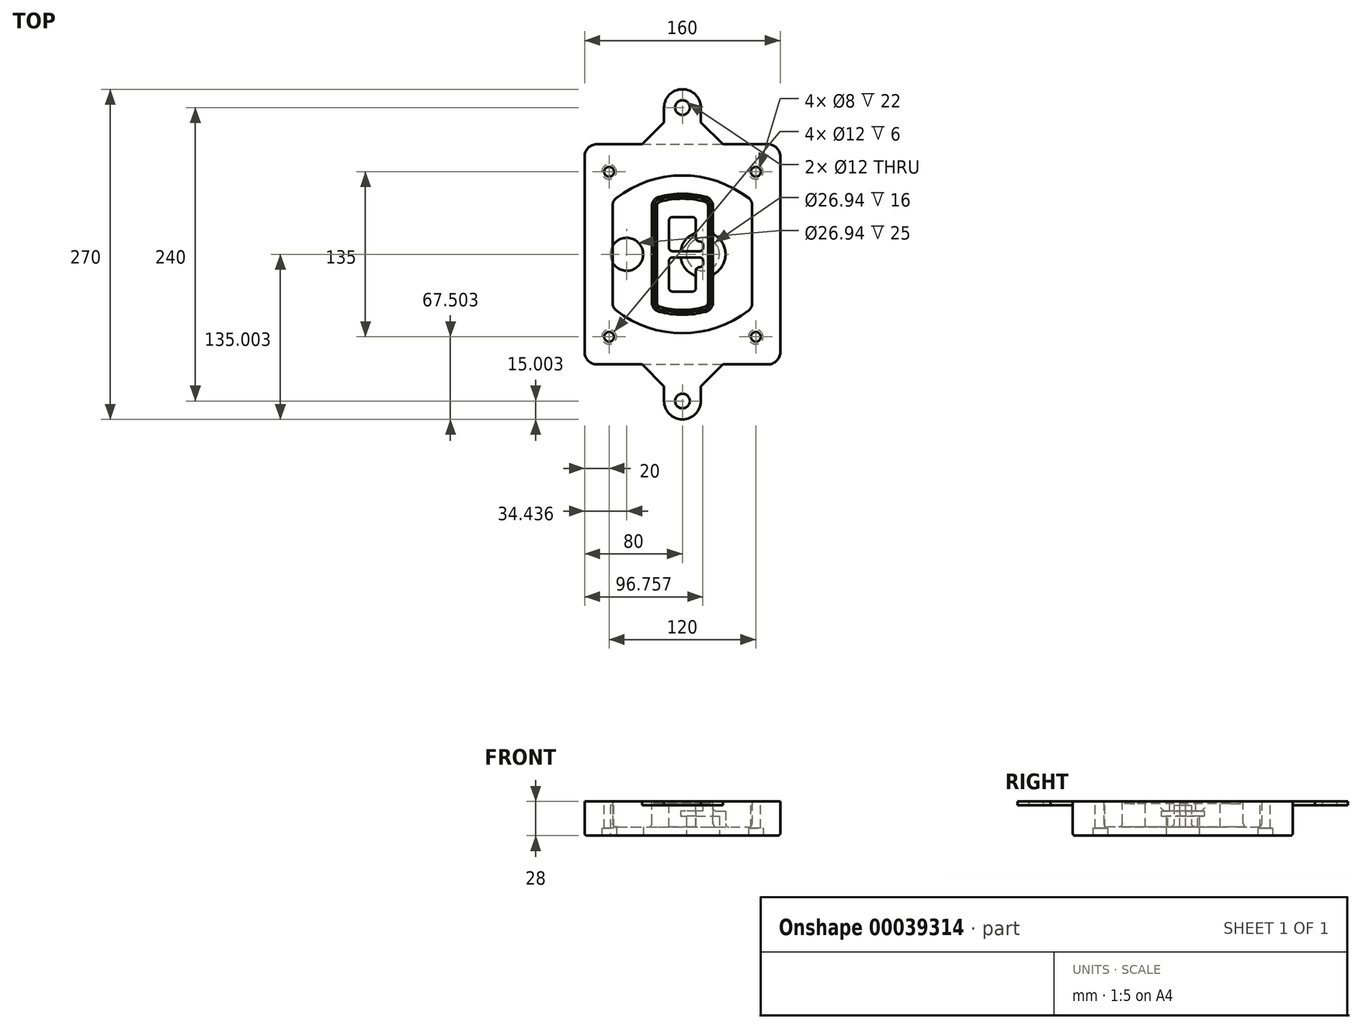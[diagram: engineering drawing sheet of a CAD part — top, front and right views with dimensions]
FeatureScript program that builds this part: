
annotation { "Feature Type Name" : "Feature", "Feature Type Description" : "" }
export const myFeature = defineFeature(function(context is Context, id is Id, definition is map)
    precondition{}
    {
        {
            var Q0;
            Q0=qCreatedBy(makeId("Top.planeOp"),FACE);
            var sketch = newSketch(context, id + "F0", { "sketchPlane" : qUnion([Q0])});
            skPoint(sketch, "E0.rect.middle", {"position": v(0, 0) * mm});
            skLineSegment(sketch, "E1.bottom", {"start": v(24.05, 28.38) * mm, "end": v(164.05, 28.38) * mm});
            skLineSegment(sketch, "E1.top", {"start": v(24.05, 208.38) * mm, "end": v(164.05, 208.38) * mm});
            skLineSegment(sketch, "E1.left", {"start": v(14.05, 38.38) * mm, "end": v(14.05, 198.38) * mm});
            skLineSegment(sketch, "E1.right", {"start": v(174.05, 38.38) * mm, "end": v(174.05, 198.38) * mm});
            skLineSegment(sketch, "E2", {"start": v(14.05, 208.38) * mm, "end": v(174.05, 28.38) * mm, "construction": true});
            skLineSegment(sketch, "E3", {"start": v(174.05, 208.38) * mm, "end": v(14.05, 28.38) * mm, "construction": true});
            skCircle(sketch, "E4", {"center": v(34.05, 185.88) * mm, "radius": 4 * mm});
            skCircle(sketch, "E5", {"center": v(154.05, 185.88) * mm, "radius": 4 * mm});
            skCircle(sketch, "E6", {"center": v(154.05, 50.88) * mm, "radius": 4 * mm});
            skCircle(sketch, "E7", {"center": v(34.05, 50.88) * mm, "radius": 4 * mm});
            skLineSegment(sketch, "E8", {"start": v(34.05, 185.88) * mm, "end": v(154.05, 185.88) * mm, "construction": true});
            skLineSegment(sketch, "E9", {"start": v(154.05, 185.88) * mm, "end": v(154.05, 50.88) * mm, "construction": true});
            skLineSegment(sketch, "E10", {"start": v(154.05, 50.88) * mm, "end": v(34.05, 50.88) * mm, "construction": true});
            skLineSegment(sketch, "E11", {"start": v(34.05, 50.88) * mm, "end": v(34.05, 185.88) * mm, "construction": true});
            skLineSegment(sketch, "E12", {"start": v(34.05, 158.68) * mm, "end": v(34.05, 78.09) * mm});
            skLineSegment(sketch, "E13", {"start": v(154.05, 158.68) * mm, "end": v(154.05, 78.09) * mm});
            skArc(sketch, "E14", {"start": v(150.2, 166.56) * mm, "mid": v(94.05, 185.88) * mm, "end": v(37.9, 166.56) * mm});
            skArc(sketch, "E15", {"start": v(37.9, 70.2) * mm, "mid": v(94.05, 50.88) * mm, "end": v(150.2, 70.2) * mm});
            skLineSegment(sketch, "E16", {"start": v(34.05, 118.38) * mm, "end": v(154.05, 118.38) * mm, "construction": true});
            skPoint(sketch, "E17.visualSharp", {"position": v(34.05, 73.38) * mm});
            skArc(sketch, "E17.filletArc", {"start": v(34.05, 78.09) * mm, "mid": v(35.06, 73.7) * mm, "end": v(37.9, 70.2) * mm});
            skPoint(sketch, "E18.visualSharp", {"position": v(34.05, 163.38) * mm});
            skArc(sketch, "E18.filletArc", {"start": v(37.9, 166.56) * mm, "mid": v(35.06, 163.06) * mm, "end": v(34.05, 158.68) * mm});
            skPoint(sketch, "E19.visualSharp", {"position": v(154.05, 163.38) * mm});
            skArc(sketch, "E19.filletArc", {"start": v(154.05, 158.68) * mm, "mid": v(153.04, 163.06) * mm, "end": v(150.2, 166.56) * mm});
            skPoint(sketch, "E20.visualSharp", {"position": v(154.05, 73.38) * mm});
            skArc(sketch, "E20.filletArc", {"start": v(150.2, 70.2) * mm, "mid": v(153.04, 73.7) * mm, "end": v(154.05, 78.09) * mm});
            skPoint(sketch, "E21.visualSharp", {"position": v(14.05, 208.38) * mm});
            skArc(sketch, "E21.filletArc", {"start": v(24.05, 208.38) * mm, "mid": v(16.98, 205.45) * mm, "end": v(14.05, 198.38) * mm});
            skPoint(sketch, "E22.visualSharp", {"position": v(174.05, 208.38) * mm});
            skArc(sketch, "E22.filletArc", {"start": v(174.05, 198.38) * mm, "mid": v(171.12, 205.45) * mm, "end": v(164.05, 208.38) * mm});
            skPoint(sketch, "E23.visualSharp", {"position": v(174.05, 28.38) * mm});
            skArc(sketch, "E23.filletArc", {"start": v(164.05, 28.38) * mm, "mid": v(171.12, 31.31) * mm, "end": v(174.05, 38.38) * mm});
            skPoint(sketch, "E24.visualSharp", {"position": v(14.05, 28.38) * mm});
            skArc(sketch, "E24.filletArc", {"start": v(14.05, 38.38) * mm, "mid": v(16.98, 31.31) * mm, "end": v(24.05, 28.38) * mm});
            skArc(sketch, "E25.0", {"start": v(151.05, 158.68) * mm, "mid": v(150.34, 161.75) * mm, "end": v(148.36, 164.2) * mm});
            skLineSegment(sketch, "E25.1", {"start": v(151.05, 158.68) * mm, "end": v(151.05, 78.09) * mm});
            skArc(sketch, "E25.2", {"start": v(148.36, 72.57) * mm, "mid": v(150.34, 75.02) * mm, "end": v(151.05, 78.09) * mm});
            skArc(sketch, "E25.3", {"start": v(39.74, 72.57) * mm, "mid": v(94.05, 53.88) * mm, "end": v(148.36, 72.57) * mm});
            skArc(sketch, "E25.4", {"start": v(37.05, 78.09) * mm, "mid": v(37.76, 75.02) * mm, "end": v(39.74, 72.57) * mm});
            skArc(sketch, "E25.5", {"start": v(148.36, 164.2) * mm, "mid": v(94.05, 182.88) * mm, "end": v(39.74, 164.2) * mm});
            skLineSegment(sketch, "E25.6", {"start": v(37.05, 158.68) * mm, "end": v(37.05, 78.09) * mm});
            skArc(sketch, "E25.7", {"start": v(39.74, 164.2) * mm, "mid": v(37.76, 161.75) * mm, "end": v(37.05, 158.68) * mm});
            skArc(sketch, "E26.0", {"start": v(35.43, 169.71) * mm, "mid": v(31.47, 164.82) * mm, "end": v(30.05, 158.68) * mm});
            skArc(sketch, "E26.1", {"start": v(152.67, 169.71) * mm, "mid": v(94.05, 189.88) * mm, "end": v(35.43, 169.71) * mm});
            skArc(sketch, "E26.2", {"start": v(158.05, 158.68) * mm, "mid": v(156.63, 164.82) * mm, "end": v(152.67, 169.71) * mm});
            skLineSegment(sketch, "E26.3", {"start": v(158.05, 158.68) * mm, "end": v(158.05, 78.09) * mm});
            skArc(sketch, "E26.4", {"start": v(152.67, 67.05) * mm, "mid": v(156.63, 71.95) * mm, "end": v(158.05, 78.09) * mm});
            skLineSegment(sketch, "E26.5", {"start": v(30.05, 158.68) * mm, "end": v(30.05, 78.09) * mm});
            skArc(sketch, "E26.6", {"start": v(35.43, 67.05) * mm, "mid": v(94.05, 46.88) * mm, "end": v(152.67, 67.05) * mm});
            skArc(sketch, "E26.7", {"start": v(30.05, 78.09) * mm, "mid": v(31.47, 71.95) * mm, "end": v(35.43, 67.05) * mm});
            skSolve(sketch);
        }
        {
            var Q0;
            Q0=makeQuery(id+"F0.imprint","IMPRINT",FACE,{"disambiguationData":[TD([[makeQuery(id+"F0.imprint","IMPRINT",EDGE,{"derivedFrom":sQuery(id+"F0.wireOp",EDGE,"E1.bottom")}),1.0]])]});
            var Q1;
            Q1=makeQuery(id+"F0.imprint","IMPRINT",FACE,{"disambiguationData":[TD([[makeQuery(id+"F0.imprint","IMPRINT",EDGE,{"derivedFrom":sQuery(id+"F0.wireOp",EDGE,"E12")}),1.0]])]});
            var Q2;
            Q2=makeQuery(id+"F0.imprint","IMPRINT",FACE,{"disambiguationData":[TD([[makeQuery(id+"F0.imprint","IMPRINT",EDGE,{"derivedFrom":sQuery(id+"F0.wireOp",EDGE,"E25.0")}),1.0]])]});
            var Q3;
            Q3=makeQuery(id+"F0.imprint","IMPRINT",FACE,{"disambiguationData":[TD([[makeQuery(id+"F0.imprint","IMPRINT",EDGE,{"derivedFrom":sQuery(id+"F0.wireOp",EDGE,"E12")}),-1.0]])]});
            extrude(context, id + "F1", {"entities" : qUnion([Q0, Q1, Q2, Q3]), "oppositeDirection" : true, "depth" : 25 * mm});
        }
        {
            var Q0;
            Q0=makeQuery(id+"F0.imprint","IMPRINT",FACE,{"disambiguationData":[TD([[makeQuery(id+"F0.imprint","IMPRINT",EDGE,{"derivedFrom":sQuery(id+"F0.wireOp",EDGE,"E12")}),1.0]])]});
            extrude(context, id + "F2", {"entities" : qUnion([Q0]), "operationType" : NewBodyOperationType.ADD, "depth" : 3 * mm});
        }
        {
            var Q0;
            Q0=makeQuery(id+"F0.imprint","IMPRINT",FACE,{"disambiguationData":[TD([[makeQuery(id+"F0.imprint","IMPRINT",EDGE,{"derivedFrom":sQuery(id+"F0.wireOp",EDGE,"E25.0")}),1.0]])]});
            extrude(context, id + "F3", {"entities" : qUnion([Q0]), "operationType" : NewBodyOperationType.REMOVE, "oppositeDirection" : true, "depth" : 18 * mm});
        }
        {
            var Q0;
            Q0=makeQuery(id+"F2.opExtrude","CAP_FACE",FACE,{"disambiguationData":[OSD([sQuery(id+"F0.wireOp",EDGE,"E12"),sQuery(id+"F0.wireOp",EDGE,"E13"),sQuery(id+"F0.wireOp",EDGE,"E14"),sQuery(id+"F0.wireOp",EDGE,"E15"),sQuery(id+"F0.wireOp",EDGE,"E17.filletArc"),sQuery(id+"F0.wireOp",EDGE,"E18.filletArc"),sQuery(id+"F0.wireOp",EDGE,"E19.filletArc"),sQuery(id+"F0.wireOp",EDGE,"E20.filletArc"),sQuery(id+"F0.wireOp",EDGE,"E25.0"),sQuery(id+"F0.wireOp",EDGE,"E25.1"),sQuery(id+"F0.wireOp",EDGE,"E25.2"),sQuery(id+"F0.wireOp",EDGE,"E25.3"),sQuery(id+"F0.wireOp",EDGE,"E25.4"),sQuery(id+"F0.wireOp",EDGE,"E25.5"),sQuery(id+"F0.wireOp",EDGE,"E25.6"),sQuery(id+"F0.wireOp",EDGE,"E25.7")])],"isStart":false});
            var sketch = newSketch(context, id + "F4", { "sketchPlane" : qUnion([Q0])});
            skArc(sketch, "E27.0", {"start": v(74.97, 71.41) * mm, "mid": v(94.05, 68.88) * mm, "end": v(113.13, 71.41) * mm});
            skArc(sketch, "E28.0", {"start": v(113.13, 165.35) * mm, "mid": v(94.05, 167.88) * mm, "end": v(74.97, 165.35) * mm});
            skLineSegment(sketch, "E29", {"start": v(69.05, 157.63) * mm, "end": v(69.05, 79.14) * mm});
            skLineSegment(sketch, "E30", {"start": v(119.05, 157.63) * mm, "end": v(119.05, 79.14) * mm});
            skLineSegment(sketch, "E31", {"start": v(69.05, 163.48) * mm, "end": v(119.05, 163.48) * mm, "construction": true});
            skLineSegment(sketch, "E32", {"start": v(69.05, 73.28) * mm, "end": v(119.05, 73.28) * mm, "construction": true});
            skPoint(sketch, "E33.visualSharp", {"position": v(69.05, 163.48) * mm});
            skArc(sketch, "E33.filletArc", {"start": v(74.97, 165.35) * mm, "mid": v(70.7, 162.5) * mm, "end": v(69.05, 157.63) * mm});
            skPoint(sketch, "E34.visualSharp", {"position": v(119.05, 163.48) * mm});
            skArc(sketch, "E34.filletArc", {"start": v(119.05, 157.63) * mm, "mid": v(117.4, 162.5) * mm, "end": v(113.13, 165.35) * mm});
            skPoint(sketch, "E35.visualSharp", {"position": v(119.05, 73.28) * mm});
            skArc(sketch, "E35.filletArc", {"start": v(113.13, 71.41) * mm, "mid": v(117.4, 74.27) * mm, "end": v(119.05, 79.14) * mm});
            skPoint(sketch, "E36.visualSharp", {"position": v(69.05, 73.28) * mm});
            skArc(sketch, "E36.filletArc", {"start": v(69.05, 79.14) * mm, "mid": v(70.7, 74.27) * mm, "end": v(74.97, 71.41) * mm});
            skArc(sketch, "E37.0", {"start": v(148.36, 164.2) * mm, "mid": v(94.05, 182.88) * mm, "end": v(39.74, 164.2) * mm});
            skArc(sketch, "E37.1", {"start": v(39.74, 164.2) * mm, "mid": v(37.76, 161.75) * mm, "end": v(37.05, 158.68) * mm});
            skLineSegment(sketch, "E37.2", {"start": v(37.05, 158.68) * mm, "end": v(37.05, 78.09) * mm});
            skArc(sketch, "E37.3", {"start": v(37.05, 78.09) * mm, "mid": v(37.76, 75.02) * mm, "end": v(39.74, 72.57) * mm});
            skArc(sketch, "E37.4", {"start": v(39.74, 72.57) * mm, "mid": v(94.05, 53.88) * mm, "end": v(148.36, 72.57) * mm});
            skArc(sketch, "E37.5", {"start": v(148.36, 72.57) * mm, "mid": v(150.34, 75.02) * mm, "end": v(151.05, 78.09) * mm});
            skLineSegment(sketch, "E37.6", {"start": v(151.05, 158.68) * mm, "end": v(151.05, 78.09) * mm});
            skArc(sketch, "E37.7", {"start": v(151.05, 158.68) * mm, "mid": v(150.34, 161.75) * mm, "end": v(148.36, 164.2) * mm});
            skLineSegment(sketch, "E38.0", {"start": v(117.05, 157.63) * mm, "end": v(117.05, 79.14) * mm});
            skArc(sketch, "E38.1", {"start": v(112.61, 73.34) * mm, "mid": v(115.81, 75.49) * mm, "end": v(117.05, 79.14) * mm});
            skArc(sketch, "E38.2", {"start": v(75.49, 73.34) * mm, "mid": v(94.05, 70.88) * mm, "end": v(112.61, 73.34) * mm});
            skArc(sketch, "E38.3", {"start": v(71.05, 79.14) * mm, "mid": v(72.29, 75.49) * mm, "end": v(75.49, 73.34) * mm});
            skLineSegment(sketch, "E38.4", {"start": v(71.05, 157.63) * mm, "end": v(71.05, 79.14) * mm});
            skArc(sketch, "E38.5", {"start": v(117.05, 157.63) * mm, "mid": v(115.81, 161.28) * mm, "end": v(112.61, 163.42) * mm});
            skArc(sketch, "E38.6", {"start": v(75.49, 163.42) * mm, "mid": v(72.29, 161.28) * mm, "end": v(71.05, 157.63) * mm});
            skArc(sketch, "E38.7", {"start": v(112.61, 163.42) * mm, "mid": v(94.05, 165.88) * mm, "end": v(75.49, 163.42) * mm});
            skArc(sketch, "E39.0", {"start": v(115.05, 157.63) * mm, "mid": v(114.23, 160.06) * mm, "end": v(112.1, 161.5) * mm});
            skLineSegment(sketch, "E39.1", {"start": v(115.05, 157.63) * mm, "end": v(115.05, 79.14) * mm});
            skArc(sketch, "E39.2", {"start": v(112.1, 75.27) * mm, "mid": v(114.23, 76.7) * mm, "end": v(115.05, 79.14) * mm});
            skArc(sketch, "E39.3", {"start": v(76, 75.27) * mm, "mid": v(94.05, 72.88) * mm, "end": v(112.1, 75.27) * mm});
            skArc(sketch, "E39.4", {"start": v(73.05, 79.14) * mm, "mid": v(73.87, 76.7) * mm, "end": v(76, 75.27) * mm});
            skArc(sketch, "E39.5", {"start": v(112.1, 161.5) * mm, "mid": v(94.05, 163.88) * mm, "end": v(76, 161.5) * mm});
            skLineSegment(sketch, "E39.6", {"start": v(73.05, 157.63) * mm, "end": v(73.05, 79.14) * mm});
            skArc(sketch, "E39.7", {"start": v(76, 161.5) * mm, "mid": v(73.87, 160.06) * mm, "end": v(73.05, 157.63) * mm});
            skLineSegment(sketch, "E40", {"start": v(69.05, 118.38) * mm, "end": v(119.05, 118.38) * mm, "construction": true});
            skLineSegment(sketch, "E41", {"start": v(83.05, 123.88) * mm, "end": v(83.05, 145.88) * mm});
            skLineSegment(sketch, "E42", {"start": v(86.05, 148.88) * mm, "end": v(102.05, 148.88) * mm});
            skLineSegment(sketch, "E43", {"start": v(105.05, 145.88) * mm, "end": v(105.05, 131.88) * mm});
            skLineSegment(sketch, "E44", {"start": v(108.05, 128.88) * mm, "end": v(108.05, 128.88) * mm});
            skLineSegment(sketch, "E45", {"start": v(111.05, 125.88) * mm, "end": v(111.05, 123.88) * mm});
            skLineSegment(sketch, "E46", {"start": v(108.05, 120.88) * mm, "end": v(86.05, 120.88) * mm});
            skPoint(sketch, "E47.visualSharp", {"position": v(83.05, 148.88) * mm});
            skArc(sketch, "E47.filletArc", {"start": v(86.05, 148.88) * mm, "mid": v(83.93, 148) * mm, "end": v(83.05, 145.88) * mm});
            skPoint(sketch, "E48.visualSharp", {"position": v(105.05, 148.88) * mm});
            skArc(sketch, "E48.filletArc", {"start": v(105.05, 145.88) * mm, "mid": v(104.17, 148) * mm, "end": v(102.05, 148.88) * mm});
            skPoint(sketch, "E49.visualSharp", {"position": v(105.05, 128.88) * mm});
            skArc(sketch, "E49.filletArc", {"start": v(105.05, 131.88) * mm, "mid": v(105.93, 129.76) * mm, "end": v(108.05, 128.88) * mm});
            skPoint(sketch, "E50.visualSharp", {"position": v(111.05, 128.88) * mm});
            skArc(sketch, "E50.filletArc", {"start": v(111.05, 125.88) * mm, "mid": v(110.17, 128) * mm, "end": v(108.05, 128.88) * mm});
            skPoint(sketch, "E51.visualSharp", {"position": v(111.05, 120.88) * mm});
            skArc(sketch, "E51.filletArc", {"start": v(108.05, 120.88) * mm, "mid": v(110.17, 121.76) * mm, "end": v(111.05, 123.88) * mm});
            skPoint(sketch, "E52.visualSharp", {"position": v(83.05, 120.88) * mm});
            skArc(sketch, "E52.filletArc", {"start": v(83.05, 123.88) * mm, "mid": v(83.93, 121.76) * mm, "end": v(86.05, 120.88) * mm});
            skLineSegment(sketch, "E53.0.MirrorCS", {"start": v(108.05, 115.88) * mm, "end": v(86.05, 115.88) * mm});
            skArc(sketch, "E54.0.MirrorCS", {"start": v(83.05, 112.88) * mm, "mid": v(83.93, 115) * mm, "end": v(86.05, 115.88) * mm});
            skLineSegment(sketch, "E55.0.MirrorCS", {"start": v(83.05, 112.88) * mm, "end": v(83.05, 90.88) * mm});
            skArc(sketch, "E56.0.MirrorCS", {"start": v(86.05, 87.88) * mm, "mid": v(83.93, 88.76) * mm, "end": v(83.05, 90.88) * mm});
            skLineSegment(sketch, "E57.0.MirrorCS", {"start": v(86.05, 87.88) * mm, "end": v(102.05, 87.88) * mm});
            skArc(sketch, "E58.0.MirrorCS", {"start": v(105.05, 90.88) * mm, "mid": v(104.17, 88.76) * mm, "end": v(102.05, 87.88) * mm});
            skLineSegment(sketch, "E59.0.MirrorCS", {"start": v(105.05, 90.88) * mm, "end": v(105.05, 104.88) * mm});
            skArc(sketch, "E60.0.MirrorCS", {"start": v(105.05, 104.88) * mm, "mid": v(105.93, 107) * mm, "end": v(108.05, 107.88) * mm});
            skArc(sketch, "E61.0.MirrorCS", {"start": v(111.05, 110.88) * mm, "mid": v(110.17, 108.76) * mm, "end": v(108.05, 107.88) * mm});
            skLineSegment(sketch, "E62.0.MirrorCS", {"start": v(111.05, 110.88) * mm, "end": v(111.05, 112.88) * mm});
            skArc(sketch, "E63.0.MirrorCS", {"start": v(108.05, 115.88) * mm, "mid": v(110.17, 115) * mm, "end": v(111.05, 112.88) * mm});
            skSolve(sketch);
        }
        {
            var Q0;
            Q0=makeQuery(id+"F4.imprint","IMPRINT",FACE,{"disambiguationData":[TD([[makeQuery(id+"F4.imprint","IMPRINT",EDGE,{"derivedFrom":sQuery(id+"F4.wireOp",EDGE,"E27.0")}),1.0]])]});
            var Q1;
            Q1=makeQuery(id+"F4.imprint","IMPRINT",FACE,{"disambiguationData":[TD([[makeQuery(id+"F4.imprint","IMPRINT",EDGE,{"derivedFrom":sQuery(id+"F4.wireOp",EDGE,"E38.0")}),-1.0]])]});
            var Q2;
            Q2=makeQuery(id+"F4.imprint","IMPRINT",FACE,{"disambiguationData":[TD([[makeQuery(id+"F4.imprint","IMPRINT",EDGE,{"derivedFrom":sQuery(id+"F4.wireOp",EDGE,"E39.0")}),1.0]])]});
            extrude(context, id + "F5", {"entities" : qUnion([Q0, Q1, Q2]), "operationType" : NewBodyOperationType.ADD, "endBound" : BoundingType.UP_TO_NEXT, "oppositeDirection" : true, "depth" : 25 * mm});
        }
        {
            var Q0;
            Q0=makeQuery(id+"F4.imprint","IMPRINT",FACE,{"disambiguationData":[TD([[makeQuery(id+"F4.imprint","IMPRINT",EDGE,{"derivedFrom":sQuery(id+"F4.wireOp",EDGE,"E38.0")}),-1.0]])]});
            extrude(context, id + "F6", {"entities" : qUnion([Q0]), "operationType" : NewBodyOperationType.REMOVE, "oppositeDirection" : true, "depth" : 2 * mm});
        }
        {
            var Q0;
            Q0=makeQuery(id+"F1.opExtrude","CAP_FACE",FACE,{"disambiguationData":[OSD([sQuery(id+"F0.wireOp",EDGE,"E1.bottom"),sQuery(id+"F0.wireOp",EDGE,"E1.top"),sQuery(id+"F0.wireOp",EDGE,"E1.left"),sQuery(id+"F0.wireOp",EDGE,"E1.right"),sQuery(id+"F0.wireOp",EDGE,"E4"),sQuery(id+"F0.wireOp",EDGE,"E5"),sQuery(id+"F0.wireOp",EDGE,"E6"),sQuery(id+"F0.wireOp",EDGE,"E7"),sQuery(id+"F0.wireOp",EDGE,"E21.filletArc"),sQuery(id+"F0.wireOp",EDGE,"E22.filletArc"),sQuery(id+"F0.wireOp",EDGE,"E23.filletArc"),sQuery(id+"F0.wireOp",EDGE,"E24.filletArc")])],"isStart":false});
            var sketch = newSketch(context, id + "F7", { "sketchPlane" : qUnion([Q0])});
            skCircle(sketch, "E64", {"center": v(110.8, -118.38) * mm, "radius": 13.47 * mm});
            skCircle(sketch, "E65", {"center": v(48.49, -118.38) * mm, "radius": 13.47 * mm});
            skLineSegment(sketch, "E66", {"start": v(174.05, -118.38) * mm, "end": v(14.05, -118.38) * mm});
            skCircle(sketch, "E67", {"center": v(110.8, -118.38) * mm, "radius": 18.47 * mm});
            skCircle(sketch, "E68", {"center": v(154.05, -185.88) * mm, "radius": 6 * mm});
            skCircle(sketch, "E69", {"center": v(34.05, -185.88) * mm, "radius": 6 * mm});
            skCircle(sketch, "E70", {"center": v(34.05, -50.88) * mm, "radius": 6 * mm});
            skCircle(sketch, "E71", {"center": v(154.05, -50.88) * mm, "radius": 6 * mm});
            skSolve(sketch);
        }
        {
            var Q0;
            {var subQ1=sQuery(id+"F7.wireOp",EDGE,"E66");var subQ4=sQuery(id+"F7.wireOp",EDGE,"E64");var subQ6=makeQuery(id+"F7.imprint","INTERSECT",VERTEX,{"disambiguationData":[OD(0.0)],"derivedFrom":[subQ4,subQ1]});Q0=makeQuery(id+"F7.imprint","IMPRINT",FACE,{"disambiguationData":[TD([[makeQuery(id+"F7.imprint","IMPRINT",EDGE,{"disambiguationData":[TD([[subQ6,-1.0]])],"derivedFrom":subQ4}),-1.0]])]});}
            var Q1;
            {var subQ0=sQuery(id+"F7.wireOp",EDGE,"E66");var subQ1=sQuery(id+"F7.wireOp",EDGE,"E64");var subQ3=makeQuery(id+"F7.imprint","INTERSECT",VERTEX,{"disambiguationData":[OD(0.0)],"derivedFrom":[subQ1,subQ0]});Q1=makeQuery(id+"F7.imprint","IMPRINT",FACE,{"disambiguationData":[TD([[makeQuery(id+"F7.imprint","IMPRINT",EDGE,{"disambiguationData":[TD([[subQ3,-1.0]])],"derivedFrom":subQ1}),1.0]])]});}
            var Q2;
            {var subQ0=sQuery(id+"F7.wireOp",EDGE,"E66");var subQ1=sQuery(id+"F7.wireOp",EDGE,"E64");var subQ3=makeQuery(id+"F7.imprint","INTERSECT",VERTEX,{"disambiguationData":[OD(0.0)],"derivedFrom":[subQ1,subQ0]});Q2=makeQuery(id+"F7.imprint","IMPRINT",FACE,{"disambiguationData":[TD([[makeQuery(id+"F7.imprint","IMPRINT",EDGE,{"disambiguationData":[TD([[subQ3,1.0]])],"derivedFrom":subQ1}),1.0]])]});}
            var Q3;
            {var subQ1=sQuery(id+"F7.wireOp",EDGE,"E66");var subQ4=sQuery(id+"F7.wireOp",EDGE,"E64");var subQ6=makeQuery(id+"F7.imprint","INTERSECT",VERTEX,{"disambiguationData":[OD(0.0)],"derivedFrom":[subQ4,subQ1]});Q3=makeQuery(id+"F7.imprint","IMPRINT",FACE,{"disambiguationData":[TD([[makeQuery(id+"F7.imprint","IMPRINT",EDGE,{"disambiguationData":[TD([[subQ6,1.0]])],"derivedFrom":subQ4}),-1.0]])]});}
            extrude(context, id + "F8", {"entities" : qUnion([Q0, Q1, Q2, Q3]), "operationType" : NewBodyOperationType.ADD, "oppositeDirection" : true, "depth" : 20 * mm});
        }
        {
            var Q0;
            {var subQ0=sQuery(id+"F7.wireOp",EDGE,"E66");var subQ1=sQuery(id+"F7.wireOp",EDGE,"E64");var subQ3=makeQuery(id+"F7.imprint","INTERSECT",VERTEX,{"disambiguationData":[OD(0.0)],"derivedFrom":[subQ1,subQ0]});Q0=makeQuery(id+"F7.imprint","IMPRINT",FACE,{"disambiguationData":[TD([[makeQuery(id+"F7.imprint","IMPRINT",EDGE,{"disambiguationData":[TD([[subQ3,-1.0]])],"derivedFrom":subQ1}),1.0]])]});}
            var Q1;
            {var subQ0=sQuery(id+"F7.wireOp",EDGE,"E66");var subQ1=sQuery(id+"F7.wireOp",EDGE,"E64");var subQ3=makeQuery(id+"F7.imprint","INTERSECT",VERTEX,{"disambiguationData":[OD(0.0)],"derivedFrom":[subQ1,subQ0]});Q1=makeQuery(id+"F7.imprint","IMPRINT",FACE,{"disambiguationData":[TD([[makeQuery(id+"F7.imprint","IMPRINT",EDGE,{"disambiguationData":[TD([[subQ3,1.0]])],"derivedFrom":subQ1}),1.0]])]});}
            extrude(context, id + "F9", {"entities" : qUnion([Q0, Q1]), "operationType" : NewBodyOperationType.REMOVE, "oppositeDirection" : true, "depth" : 16 * mm});
        }
        {
            var Q0;
            {var subQ0=sQuery(id+"F7.wireOp",EDGE,"E66");var subQ1=sQuery(id+"F7.wireOp",EDGE,"E65");var subQ3=makeQuery(id+"F7.imprint","INTERSECT",VERTEX,{"disambiguationData":[OD(0.0)],"derivedFrom":[subQ1,subQ0]});Q0=makeQuery(id+"F7.imprint","IMPRINT",FACE,{"disambiguationData":[TD([[makeQuery(id+"F7.imprint","IMPRINT",EDGE,{"disambiguationData":[TD([[subQ3,-1.0]])],"derivedFrom":subQ1}),1.0]])]});}
            var Q1;
            {var subQ0=sQuery(id+"F7.wireOp",EDGE,"E66");var subQ1=sQuery(id+"F7.wireOp",EDGE,"E65");var subQ3=makeQuery(id+"F7.imprint","INTERSECT",VERTEX,{"disambiguationData":[OD(0.0)],"derivedFrom":[subQ1,subQ0]});Q1=makeQuery(id+"F7.imprint","IMPRINT",FACE,{"disambiguationData":[TD([[makeQuery(id+"F7.imprint","IMPRINT",EDGE,{"disambiguationData":[TD([[subQ3,1.0]])],"derivedFrom":subQ1}),1.0]])]});}
            extrude(context, id + "F10", {"entities" : qUnion([Q0, Q1]), "operationType" : NewBodyOperationType.REMOVE, "oppositeDirection" : true, "depth" : 25 * mm});
        }
        {
            var Q0;
            Q0=makeQuery(id+"F7.imprint","IMPRINT",FACE,{"disambiguationData":[TD([[makeQuery(id+"F7.imprint","IMPRINT",EDGE,{"derivedFrom":sQuery(id+"F7.wireOp",EDGE,"E68")}),1.0]])]});
            var Q1;
            Q1=makeQuery(id+"F7.imprint","IMPRINT",FACE,{"disambiguationData":[TD([[makeQuery(id+"F7.imprint","IMPRINT",EDGE,{"derivedFrom":makeQuery(id+"F1.opExtrude","CAP_EDGE",EDGE,{"disambiguationData":[OSD([sQuery(id+"F0.wireOp",EDGE,"E5")])],"isStart":false})}),-1.0]])]});
            var Q2;
            Q2=makeQuery(id+"F7.imprint","IMPRINT",FACE,{"disambiguationData":[TD([[makeQuery(id+"F7.imprint","IMPRINT",EDGE,{"derivedFrom":sQuery(id+"F7.wireOp",EDGE,"E69")}),1.0]])]});
            var Q3;
            Q3=makeQuery(id+"F7.imprint","IMPRINT",FACE,{"disambiguationData":[TD([[makeQuery(id+"F7.imprint","IMPRINT",EDGE,{"derivedFrom":makeQuery(id+"F1.opExtrude","CAP_EDGE",EDGE,{"disambiguationData":[OSD([sQuery(id+"F0.wireOp",EDGE,"E4")])],"isStart":false})}),-1.0]])]});
            var Q4;
            Q4=makeQuery(id+"F7.imprint","IMPRINT",FACE,{"disambiguationData":[TD([[makeQuery(id+"F7.imprint","IMPRINT",EDGE,{"derivedFrom":sQuery(id+"F7.wireOp",EDGE,"E70")}),1.0]])]});
            var Q5;
            Q5=makeQuery(id+"F7.imprint","IMPRINT",FACE,{"disambiguationData":[TD([[makeQuery(id+"F7.imprint","IMPRINT",EDGE,{"derivedFrom":makeQuery(id+"F1.opExtrude","CAP_EDGE",EDGE,{"disambiguationData":[OSD([sQuery(id+"F0.wireOp",EDGE,"E7")])],"isStart":false})}),-1.0]])]});
            var Q6;
            Q6=makeQuery(id+"F7.imprint","IMPRINT",FACE,{"disambiguationData":[TD([[makeQuery(id+"F7.imprint","IMPRINT",EDGE,{"derivedFrom":sQuery(id+"F7.wireOp",EDGE,"E71")}),1.0]])]});
            var Q7;
            Q7=makeQuery(id+"F7.imprint","IMPRINT",FACE,{"disambiguationData":[TD([[makeQuery(id+"F7.imprint","IMPRINT",EDGE,{"derivedFrom":makeQuery(id+"F1.opExtrude","CAP_EDGE",EDGE,{"disambiguationData":[OSD([sQuery(id+"F0.wireOp",EDGE,"E6")])],"isStart":false})}),-1.0]])]});
            extrude(context, id + "F11", {"entities" : qUnion([Q0, Q1, Q2, Q3, Q4, Q5, Q6, Q7]), "operationType" : NewBodyOperationType.REMOVE, "oppositeDirection" : true, "depth" : 6 * mm});
        }
        {
            var Q0;
            Q0=makeQuery(id+"F9.boolean.opBoolean","COPY",FACE,{"derivedFrom":makeQuery(id+"F9.opExtrude","CAP_FACE",FACE,{"disambiguationData":[OSD([sQuery(id+"F7.wireOp",EDGE,"E64")])],"isStart":false})});
            var sketch = newSketch(context, id + "F12", { "sketchPlane" : qUnion([Q0])});
            skArc(sketch, "E72.0", {"start": v(105.05, -100.83) * mm, "mid": v(96.62, -106.56) * mm, "end": v(92.5, -115.88) * mm});
            skArc(sketch, "E72.1", {"start": v(92.5, -120.88) * mm, "mid": v(96.62, -130.2) * mm, "end": v(105.05, -135.93) * mm});
            skLineSegment(sketch, "E73", {"start": v(92.5, -120.88) * mm, "end": v(108.05, -120.88) * mm});
            skLineSegment(sketch, "E74.0", {"start": v(108.05, -115.88) * mm, "end": v(92.5, -115.88) * mm});
            skArc(sketch, "E74.1", {"start": v(108.05, -115.88) * mm, "mid": v(110.17, -115) * mm, "end": v(111.05, -112.88) * mm});
            skLineSegment(sketch, "E74.2", {"start": v(111.05, -110.88) * mm, "end": v(111.05, -112.88) * mm});
            skArc(sketch, "E74.3", {"start": v(111.05, -110.88) * mm, "mid": v(110.17, -108.76) * mm, "end": v(108.05, -107.88) * mm});
            skArc(sketch, "E74.4", {"start": v(105.05, -104.88) * mm, "mid": v(105.93, -107) * mm, "end": v(108.05, -107.88) * mm});
            skLineSegment(sketch, "E74.5", {"start": v(105.05, -100.83) * mm, "end": v(105.05, -104.88) * mm});
            skLineSegment(sketch, "E74.7", {"start": v(108.05, -120.88) * mm, "end": v(92.5, -120.88) * mm});
            skArc(sketch, "E74.8", {"start": v(108.05, -120.88) * mm, "mid": v(110.17, -121.76) * mm, "end": v(111.05, -123.88) * mm});
            skLineSegment(sketch, "E74.9", {"start": v(111.05, -125.88) * mm, "end": v(111.05, -123.88) * mm});
            skArc(sketch, "E74.10", {"start": v(111.05, -125.88) * mm, "mid": v(110.17, -128) * mm, "end": v(108.05, -128.88) * mm});
            skArc(sketch, "E74.11", {"start": v(105.05, -131.88) * mm, "mid": v(105.93, -129.76) * mm, "end": v(108.05, -128.88) * mm});
            skLineSegment(sketch, "E74.12", {"start": v(105.05, -135.93) * mm, "end": v(105.05, -131.88) * mm});
            skPoint(sketch, "E75.orphan", {"position": v(105.05, -145.88) * mm});
            skPoint(sketch, "E76.orphan", {"position": v(86.05, -120.88) * mm});
            skPoint(sketch, "E77.orphan", {"position": v(86.05, -115.88) * mm});
            skPoint(sketch, "E78.orphan", {"position": v(105.05, -90.88) * mm});
            skSolve(sketch);
        }
        {
            var Q0;
            {var subQ7=sQuery(id+"F12.wireOp",EDGE,"E72.0");var subQ14=sQuery(id+"F12.wireOp",EDGE,"E72.1");var subQ16=sQuery(id+"F12.wireOp",EDGE,"E74.1");var subQ18=sQuery(id+"F12.wireOp",EDGE,"E74.8");Q0=qUnion([makeQuery(id+"F12.imprint","IMPRINT",FACE,{"disambiguationData":[TD([[makeQuery(id+"F12.imprint","IMPRINT",EDGE,{"derivedFrom":subQ7}),1.0]])]}),makeQuery(id+"F12.imprint","IMPRINT",FACE,{"disambiguationData":[TD([[makeQuery(id+"F12.imprint","IMPRINT",EDGE,{"derivedFrom":subQ14}),1.0]])]}),makeQuery(id+"F12.imprint","IMPRINT",FACE,{"disambiguationData":[TD([[makeQuery(id+"F12.imprint","IMPRINT",EDGE,{"derivedFrom":subQ16}),1.0]])]}),makeQuery(id+"F12.imprint","IMPRINT",FACE,{"disambiguationData":[TD([[makeQuery(id+"F12.imprint","IMPRINT",EDGE,{"derivedFrom":subQ18}),-1.0]])]})]);}
            var Q1;
            Q1=makeQuery(id+"F5.boolean.opBoolean","SPLIT",FACE,{"disambiguationData":[TD([makeQuery(id+"F5.opExtrude","SWEPT_FACE",FACE,{"disambiguationData":[OSD([sQuery(id+"F4.wireOp",EDGE,"E41")])]})])],"derivedFrom":makeQuery(id+"F3.boolean.opBoolean","COPY",FACE,{"derivedFrom":makeQuery(id+"F3.opExtrude","CAP_FACE",FACE,{"disambiguationData":[OSD([sQuery(id+"F0.wireOp",EDGE,"E25.0"),sQuery(id+"F0.wireOp",EDGE,"E25.1"),sQuery(id+"F0.wireOp",EDGE,"E25.2"),sQuery(id+"F0.wireOp",EDGE,"E25.3"),sQuery(id+"F0.wireOp",EDGE,"E25.4"),sQuery(id+"F0.wireOp",EDGE,"E25.5"),sQuery(id+"F0.wireOp",EDGE,"E25.6"),sQuery(id+"F0.wireOp",EDGE,"E25.7")])],"isStart":false})})});
            extrude(context, id + "F13", {"entities" : qUnion([Q0]), "operationType" : NewBodyOperationType.REMOVE, "endBound" : BoundingType.UP_TO_SURFACE, "endBoundEntityFace" : qUnion([Q1]), "depth" : 25 * mm});
        }
        {
            var Q0;
            Q0=makeQuery(id+"F3.boolean.opBoolean","COPY",EDGE,{"derivedFrom":makeQuery(id+"F3.opExtrude","CAP_EDGE",EDGE,{"disambiguationData":[OSD([sQuery(id+"F0.wireOp",EDGE,"E25.6")])],"isStart":false})});
            var Q1;
            Q1=makeQuery(id+"F8.boolean.opBoolean","INTERSECT",EDGE,{"derivedFrom":[makeQuery(id+"F5.opExtrude","SWEPT_FACE",FACE,{"disambiguationData":[OSD([sQuery(id+"F4.wireOp",EDGE,"E30")])]}),makeQuery(id+"F8.opExtrude","CAP_FACE",FACE,{"disambiguationData":[OSD([sQuery(id+"F7.wireOp",EDGE,"E67")])],"isStart":false})]});
            var Q2;
            Q2=makeQuery(id+"F8.boolean.opBoolean","INTERSECT",EDGE,{"disambiguationData":[OD(1.0)],"derivedFrom":[makeQuery(id+"F5.opExtrude","SWEPT_FACE",FACE,{"disambiguationData":[OSD([sQuery(id+"F4.wireOp",EDGE,"E30")])]}),makeQuery(id+"F8.opExtrude","SWEPT_FACE",FACE,{"disambiguationData":[OSD([sQuery(id+"F7.wireOp",EDGE,"E67")])]})]});
            var Q3;
            {var subQ0=sQuery(id+"F4.wireOp",EDGE,"E30");Q3=makeQuery(id+"F8.boolean.opBoolean","SPLIT",EDGE,{"disambiguationData":[TD([makeQuery(id+"F5.opExtrude","SWEPT_FACE",FACE,{"disambiguationData":[OSD([sQuery(id+"F4.wireOp",EDGE,"E35.filletArc")])]})])],"derivedFrom":makeQuery(id+"F5.opExtrude","CAP_EDGE",EDGE,{"disambiguationData":[OSD([subQ0])],"isStart":false})});}
            var Q4;
            {var subQ0=sQuery(id+"F0.wireOp",EDGE,"E25.7");var subQ1=sQuery(id+"F0.wireOp",EDGE,"E25.1");var subQ2=sQuery(id+"F0.wireOp",EDGE,"E25.6");var subQ3=sQuery(id+"F0.wireOp",EDGE,"E25.5");var subQ4=sQuery(id+"F0.wireOp",EDGE,"E25.4");var subQ5=sQuery(id+"F0.wireOp",EDGE,"E25.0");var subQ6=sQuery(id+"F0.wireOp",EDGE,"E25.2");var subQ7=sQuery(id+"F0.wireOp",EDGE,"E25.3");Q4=makeQuery(id+"F8.boolean.opBoolean","INTERSECT",EDGE,{"derivedFrom":[makeQuery(id+"F5.boolean.opBoolean","SPLIT",FACE,{"disambiguationData":[TD([makeQuery(id+"F2.opExtrude","SWEPT_FACE",FACE,{"disambiguationData":[OSD([subQ5])]})])],"derivedFrom":makeQuery(id+"F3.boolean.opBoolean","COPY",FACE,{"derivedFrom":makeQuery(id+"F3.opExtrude","CAP_FACE",FACE,{"disambiguationData":[OSD([subQ5,subQ1,subQ6,subQ7,subQ4,subQ3,subQ2,subQ0])],"isStart":false})})}),makeQuery(id+"F8.opExtrude","SWEPT_FACE",FACE,{"disambiguationData":[OSD([sQuery(id+"F7.wireOp",EDGE,"E67")])]})]});}
            var Q5;
            Q5=makeQuery(id+"F8.boolean.opBoolean","INTERSECT",EDGE,{"disambiguationData":[OD(0.0)],"derivedFrom":[makeQuery(id+"F5.opExtrude","SWEPT_FACE",FACE,{"disambiguationData":[OSD([sQuery(id+"F4.wireOp",EDGE,"E30")])]}),makeQuery(id+"F8.opExtrude","SWEPT_FACE",FACE,{"disambiguationData":[OSD([sQuery(id+"F7.wireOp",EDGE,"E67")])]})]});
            fillet(context, id + "F14", {"entities" : qUnion([Q0, Q1, Q2, Q3, Q4, Q5]), "radius" : 3 * mm, "tangentPropagation" : true, "allowEdgeOverflow" : false});
        }
        {
            var Q0;
            Q0=makeQuery(id+"F1.opExtrude","CAP_EDGE",EDGE,{"disambiguationData":[OSD([sQuery(id+"F0.wireOp",EDGE,"E1.bottom")])],"isStart":false});
            fillet(context, id + "F15", {"entities" : qUnion([Q0]), "radius" : 2 * mm, "tangentPropagation" : true, "allowEdgeOverflow" : false});
        }
        {
            var Q0;
            {var subQ0=sQuery(id+"F0.wireOp",EDGE,"E1.bottom");var subQ1=sQuery(id+"F0.wireOp",EDGE,"E1.top");var subQ2=sQuery(id+"F0.wireOp",EDGE,"E1.left");var subQ3=sQuery(id+"F0.wireOp",EDGE,"E1.right");var subQ4=sQuery(id+"F0.wireOp",EDGE,"E4");var subQ5=sQuery(id+"F0.wireOp",EDGE,"E5");var subQ6=sQuery(id+"F0.wireOp",EDGE,"E6");var subQ7=sQuery(id+"F0.wireOp",EDGE,"E7");var subQ8=sQuery(id+"F0.wireOp",EDGE,"E21.filletArc");var subQ9=sQuery(id+"F0.wireOp",EDGE,"E22.filletArc");var subQ10=sQuery(id+"F0.wireOp",EDGE,"E23.filletArc");var subQ11=sQuery(id+"F0.wireOp",EDGE,"E24.filletArc");Q0=makeQuery(id+"F2.boolean.opBoolean","SPLIT",FACE,{"disambiguationData":[TD([makeQuery(id+"F1.opExtrude","SWEPT_FACE",FACE,{"disambiguationData":[OSD([subQ0])]})])],"derivedFrom":makeQuery(id+"F1.opExtrude","CAP_FACE",FACE,{"disambiguationData":[OSD([subQ0,subQ1,subQ2,subQ3,subQ4,subQ5,subQ6,subQ7,subQ8,subQ9,subQ10,subQ11])],"isStart":true})});}
            var sketch = newSketch(context, id + "F16", { "sketchPlane" : qUnion([Q0])});
            skLineSegment(sketch, "E79", {"start": v(94.05, 208.38) * mm, "end": v(94.05, 221.77) * mm, "construction": true});
            skCircle(sketch, "E80", {"center": v(94.05, 238.38) * mm, "radius": 15 * mm});
            skCircle(sketch, "E81", {"center": v(94.05, 238.38) * mm, "radius": 6 * mm});
            skLineSegment(sketch, "E82", {"start": v(79.05, 238.38) * mm, "end": v(79.05, 226.38) * mm});
            skLineSegment(sketch, "E83", {"start": v(79.05, 238.38) * mm, "end": v(79.05, 200.35) * mm, "construction": true});
            skLineSegment(sketch, "E84", {"start": v(79.05, 208.38) * mm, "end": v(61.05, 208.38) * mm});
            skLineSegment(sketch, "E85", {"start": v(61.05, 208.38) * mm, "end": v(79.05, 226.38) * mm});
            skLineSegment(sketch, "E86.MirrorCS", {"start": v(127.05, 208.38) * mm, "end": v(109.05, 226.38) * mm});
            skLineSegment(sketch, "E87.MirrorCS", {"start": v(109.05, 238.38) * mm, "end": v(109.05, 226.38) * mm});
            skLineSegment(sketch, "E88", {"start": v(174.05, 118.38) * mm, "end": v(185, 118.38) * mm, "construction": true});
            skPoint(sketch, "E88.endSnap0", {"position": v(174.05, 118.38) * mm});
            skLineSegment(sketch, "E89.MirrorCS", {"start": v(127.05, 28.38) * mm, "end": v(109.05, 10.38) * mm});
            skLineSegment(sketch, "E90.MirrorCS", {"start": v(61.05, 28.38) * mm, "end": v(79.05, 10.38) * mm});
            skCircle(sketch, "E91.MirrorC", {"center": v(94.05, -1.62) * mm, "radius": 15 * mm});
            skLineSegment(sketch, "E92.MirrorCS", {"start": v(79.05, -1.62) * mm, "end": v(79.05, 10.38) * mm});
            skLineSegment(sketch, "E93.MirrorCS", {"start": v(109.05, -1.62) * mm, "end": v(109.05, 10.38) * mm});
            skCircle(sketch, "E94.MirrorC", {"center": v(94.05, -1.62) * mm, "radius": 6 * mm});
            skSolve(sketch);
        }
        {
            var Q0;
            Q0 = qSketchRegion(id + "F16", true);
            var Q1;
            {var subQ3=sQuery(id+"F16.wireOp",EDGE,"E84");Q1=makeQuery(id+"F16.imprint","IMPRINT",FACE,{"disambiguationData":[TD([[makeQuery(id+"F16.imprint","IMPRINT",EDGE,{"derivedFrom":subQ3}),-1.0]])]});}
            var Q2;
            {var subQ5=sQuery(id+"F16.wireOp",EDGE,"E82");Q2=makeQuery(id+"F16.imprint","IMPRINT",FACE,{"disambiguationData":[TD([[makeQuery(id+"F16.imprint","IMPRINT",EDGE,{"derivedFrom":subQ5}),1.0]])]});}
            var Q3;
            {var subQ1=sQuery(id+"F16.wireOp",EDGE,"E89.MirrorCS");Q3=makeQuery(id+"F16.imprint","IMPRINT",FACE,{"disambiguationData":[TD([[makeQuery(id+"F16.imprint","IMPRINT",EDGE,{"derivedFrom":subQ1}),-1.0]])]});}
            var Q4;
            Q4=makeQuery(id+"F2.opExtrude","CAP_FACE",FACE,{"disambiguationData":[OSD([sQuery(id+"F0.wireOp",EDGE,"E12"),sQuery(id+"F0.wireOp",EDGE,"E13"),sQuery(id+"F0.wireOp",EDGE,"E14"),sQuery(id+"F0.wireOp",EDGE,"E15"),sQuery(id+"F0.wireOp",EDGE,"E17.filletArc"),sQuery(id+"F0.wireOp",EDGE,"E18.filletArc"),sQuery(id+"F0.wireOp",EDGE,"E19.filletArc"),sQuery(id+"F0.wireOp",EDGE,"E20.filletArc"),sQuery(id+"F0.wireOp",EDGE,"E25.0"),sQuery(id+"F0.wireOp",EDGE,"E25.1"),sQuery(id+"F0.wireOp",EDGE,"E25.2"),sQuery(id+"F0.wireOp",EDGE,"E25.3"),sQuery(id+"F0.wireOp",EDGE,"E25.4"),sQuery(id+"F0.wireOp",EDGE,"E25.5"),sQuery(id+"F0.wireOp",EDGE,"E25.6"),sQuery(id+"F0.wireOp",EDGE,"E25.7")])],"isStart":false});
            extrude(context, id + "F17", {"entities" : qUnion([Q0, Q1, Q2, Q3]), "operationType" : NewBodyOperationType.ADD, "endBound" : BoundingType.UP_TO_SURFACE, "endBoundEntityFace" : qUnion([Q4]), "depth" : 25 * mm});
        }
    });
